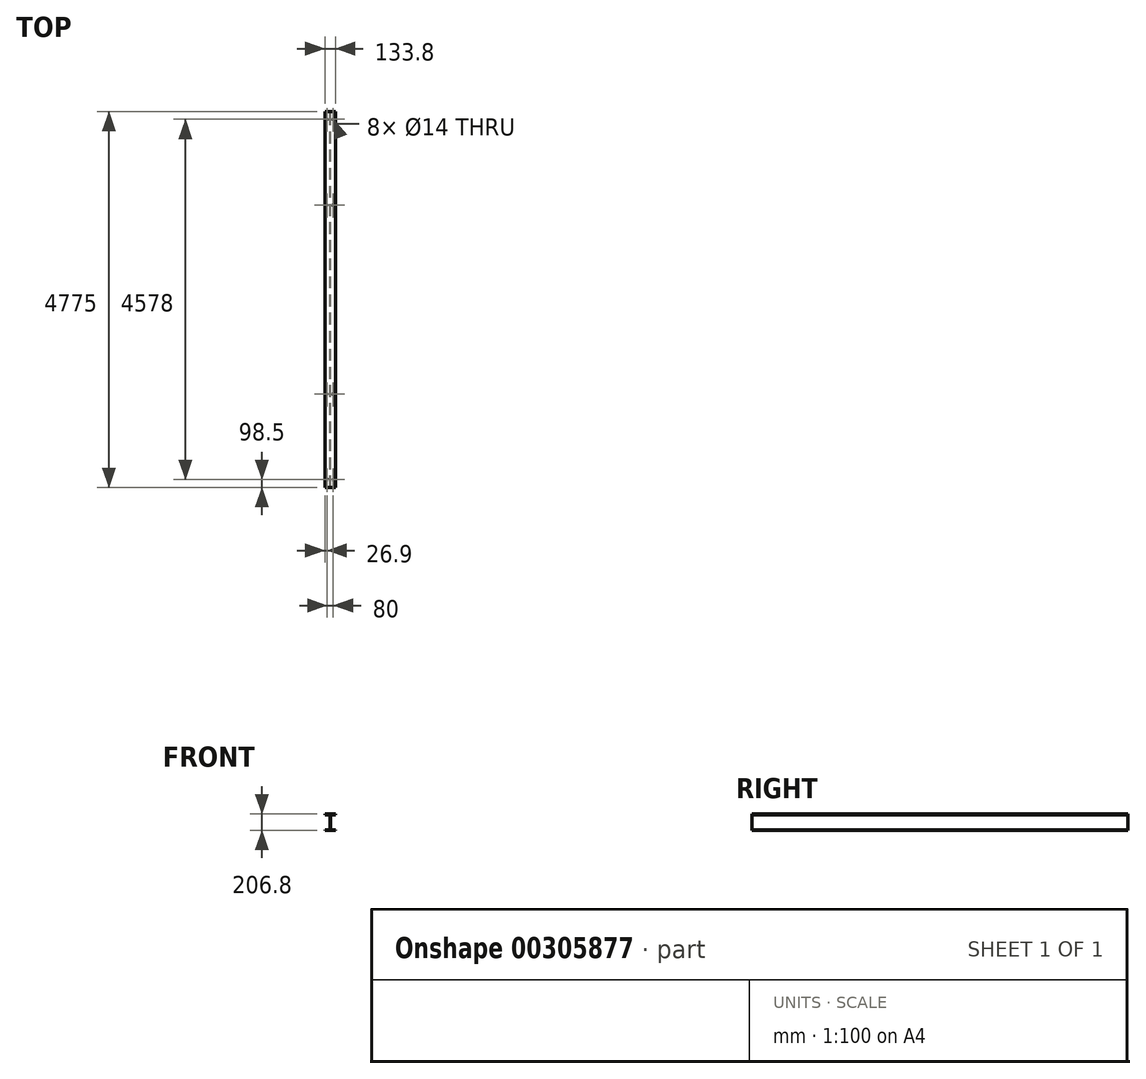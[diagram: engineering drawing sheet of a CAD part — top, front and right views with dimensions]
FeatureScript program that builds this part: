
annotation { "Feature Type Name" : "Feature", "Feature Type Description" : "" }
export const myFeature = defineFeature(function(context is Context, id is Id, definition is map)
    precondition{}
    {
        {
            var Q0;
            Q0=qCreatedBy(makeId("Front.planeOp"),FACE);
            var sketch = newSketch(context, id + "F0", { "sketchPlane" : qUnion([Q0])});
            skLineSegment(sketch, "E0.bottom", {"start": v(3.15, -24.05) * mm, "end": v(-3.15, -24.05) * mm});
            skLineSegment(sketch, "E0.top", {"start": v(3.15, 182.75) * mm, "end": v(-3.15, 182.75) * mm});
            skLineSegment(sketch, "E0.left", {"start": v(3.15, -24.05) * mm, "end": v(3.15, 182.75) * mm});
            skLineSegment(sketch, "E0.right", {"start": v(-3.15, -24.05) * mm, "end": v(-3.15, 182.75) * mm});
            skPoint(sketch, "E0.middle", {"position": v(0, 79.35) * mm});
            skLineSegment(sketch, "E1", {"start": v(0, 182.75) * mm, "end": v(0, 177.95) * mm, "construction": true});
            skLineSegment(sketch, "E2", {"start": v(0, -24.05) * mm, "end": v(0, -19.25) * mm, "construction": true});
            skLineSegment(sketch, "E3.bottom", {"start": v(66.9, 182.75) * mm, "end": v(-66.9, 182.75) * mm});
            skLineSegment(sketch, "E3.top", {"start": v(66.9, 173.15) * mm, "end": v(-66.9, 173.15) * mm});
            skLineSegment(sketch, "E3.left", {"start": v(66.9, 182.75) * mm, "end": v(66.9, 173.15) * mm});
            skLineSegment(sketch, "E3.right", {"start": v(-66.9, 182.75) * mm, "end": v(-66.9, 173.15) * mm});
            skPoint(sketch, "E3.middle", {"position": v(0, 177.95) * mm});
            skLineSegment(sketch, "E4.bottom", {"start": v(66.9, -24.05) * mm, "end": v(-66.9, -24.05) * mm});
            skLineSegment(sketch, "E4.top", {"start": v(66.9, -14.45) * mm, "end": v(-66.9, -14.45) * mm});
            skLineSegment(sketch, "E4.left", {"start": v(66.9, -24.05) * mm, "end": v(66.9, -14.45) * mm});
            skLineSegment(sketch, "E4.right", {"start": v(-66.9, -24.05) * mm, "end": v(-66.9, -14.45) * mm});
            skPoint(sketch, "E4.middle", {"position": v(0, -19.25) * mm});
            skSolve(sketch);
        }
        {
            var Q0;
            {var subQ5=sQuery(id+"F0.wireOp",EDGE,"E3.left");Q0=makeQuery(id+"F0.imprint","IMPRINT",FACE,{"disambiguationData":[TD([[makeQuery(id+"F0.imprint","IMPRINT",EDGE,{"derivedFrom":subQ5}),-1.0]])]});}
            var Q1;
            {var subQ5=sQuery(id+"F0.wireOp",EDGE,"E3.right");Q1=makeQuery(id+"F0.imprint","IMPRINT",FACE,{"disambiguationData":[TD([[makeQuery(id+"F0.imprint","IMPRINT",EDGE,{"derivedFrom":subQ5}),1.0]])]});}
            var Q2;
            {var subQ0=sQuery(id+"F0.wireOp",EDGE,"E3.bottom");var subQ1=sQuery(id+"F0.wireOp",EDGE,"E0.left");var subQ2=makeQuery(id+"F0.imprint","INTERSECT",VERTEX,{"derivedFrom":[subQ1,subQ0]});Q2=makeQuery(id+"F0.imprint","IMPRINT",FACE,{"disambiguationData":[TD([[makeQuery(id+"F0.imprint","IMPRINT",EDGE,{"disambiguationData":[TD([[subQ2,1.0]])],"derivedFrom":subQ1}),1.0]])]});}
            var Q3;
            {var subQ0=sQuery(id+"F0.wireOp",EDGE,"E4.top");var subQ1=sQuery(id+"F0.wireOp",EDGE,"E0.left");var subQ2=makeQuery(id+"F0.imprint","INTERSECT",VERTEX,{"derivedFrom":[subQ1,subQ0]});Q3=makeQuery(id+"F0.imprint","IMPRINT",FACE,{"disambiguationData":[TD([[makeQuery(id+"F0.imprint","IMPRINT",EDGE,{"disambiguationData":[TD([[subQ2,-1.0]])],"derivedFrom":subQ1}),1.0]])]});}
            var Q4;
            {var subQ5=sQuery(id+"F0.wireOp",EDGE,"E4.right");Q4=makeQuery(id+"F0.imprint","IMPRINT",FACE,{"disambiguationData":[TD([[makeQuery(id+"F0.imprint","IMPRINT",EDGE,{"derivedFrom":subQ5}),-1.0]])]});}
            var Q5;
            {var subQ0=sQuery(id+"F0.wireOp",EDGE,"E4.bottom");var subQ1=sQuery(id+"F0.wireOp",EDGE,"E0.left");var subQ2=makeQuery(id+"F0.imprint","INTERSECT",VERTEX,{"derivedFrom":[subQ1,subQ0]});Q5=makeQuery(id+"F0.imprint","IMPRINT",FACE,{"disambiguationData":[TD([[makeQuery(id+"F0.imprint","IMPRINT",EDGE,{"disambiguationData":[TD([[subQ2,-1.0]])],"derivedFrom":subQ1}),1.0]])]});}
            var Q6;
            {var subQ5=sQuery(id+"F0.wireOp",EDGE,"E4.left");Q6=makeQuery(id+"F0.imprint","IMPRINT",FACE,{"disambiguationData":[TD([[makeQuery(id+"F0.imprint","IMPRINT",EDGE,{"derivedFrom":subQ5}),1.0]])]});}
            extrude(context, id + "F1", {"entities" : qUnion([Q0, Q1, Q2, Q3, Q4, Q5, Q6]), "depth" : 4775 * mm});
        }
        {
            var Q0;
            Q0=makeQuery(id+"F1.opExtrude","SWEPT_FACE",FACE,{"disambiguationData":[OSD([sQuery(id+"F0.wireOp",EDGE,"E3.bottom")])]});
            var sketch = newSketch(context, id + "F2", { "sketchPlane" : qUnion([Q0])});
            skLineSegment(sketch, "E5.bottom", {"start": v(72.5, -4887.5) * mm, "end": v(-72.5, -4887.5) * mm});
            skLineSegment(sketch, "E5.top", {"start": v(72.5, 112.5) * mm, "end": v(-72.5, 112.5) * mm});
            skLineSegment(sketch, "E5.left", {"start": v(72.5, -4887.5) * mm, "end": v(72.5, 112.5) * mm});
            skLineSegment(sketch, "E5.right", {"start": v(-72.5, -4887.5) * mm, "end": v(-72.5, 112.5) * mm});
            skPoint(sketch, "E5.middle", {"position": v(0, -2387.5) * mm});
            skPoint(sketch, "E5.middle.positionSnap0", {"position": v(66.9, -2387.5) * mm});
            skPoint(sketch, "E5.centerSnap0", {"position": v(66.9, -2387.5) * mm});
            skLineSegment(sketch, "E6.bottom", {"start": v(40, -4887.5) * mm, "end": v(-40, -4887.5) * mm, "construction": true});
            skLineSegment(sketch, "E6.top", {"start": v(40, 112.5) * mm, "end": v(-40, 112.5) * mm, "construction": true});
            skLineSegment(sketch, "E6.left", {"start": v(40, -4887.5) * mm, "end": v(40, 112.5) * mm, "construction": true});
            skLineSegment(sketch, "E6.right", {"start": v(-40, -4887.5) * mm, "end": v(-40, 112.5) * mm, "construction": true});
            skLineSegment(sketch, "E7", {"start": v(-40, -1187.5) * mm, "end": v(40, -1187.5) * mm, "construction": true});
            skLineSegment(sketch, "E8", {"start": v(-40, -98.5) * mm, "end": v(40, -98.5) * mm, "construction": true});
            skLineSegment(sketch, "E9", {"start": v(-72.5, -2387.5) * mm, "end": v(72.5, -2387.5) * mm, "construction": true});
            skLineSegment(sketch, "E10.MirrorCS", {"start": v(-40, -3587.5) * mm, "end": v(40, -3587.5) * mm, "construction": true});
            skLineSegment(sketch, "E11.MirrorCS", {"start": v(-40, -4676.5) * mm, "end": v(40, -4676.5) * mm, "construction": true});
            skSolve(sketch);
        }
        {
            var Q0;
            Q0=sQuery(id+"F2.wireOp",VERTEX,"E8.start");
            var Q1;
            Q1=sQuery(id+"F2.wireOp",VERTEX,"E8.end");
            var Q2;
            Q2=sQuery(id+"F2.wireOp",VERTEX,"E7.start");
            var Q3;
            Q3=sQuery(id+"F2.wireOp",VERTEX,"E7.end");
            var Q4;
            Q4=sQuery(id+"F2.wireOp",VERTEX,"E10.MirrorCS.start");
            var Q5;
            Q5=sQuery(id+"F2.wireOp",VERTEX,"E10.MirrorCS.end");
            var Q6;
            Q6=sQuery(id+"F2.wireOp",VERTEX,"E11.MirrorCS.start");
            var Q7;
            Q7=sQuery(id+"F2.wireOp",VERTEX,"E11.MirrorCS.end");
            var Q8;
            Q8=makeQuery(id+"F1.opExtrude","SWEPT_BODY",BODY,{"disambiguationData":[OSD([sQuery(id+"F0.wireOp",EDGE,"E0.left"),sQuery(id+"F0.wireOp",EDGE,"E0.right"),sQuery(id+"F0.wireOp",EDGE,"E3.bottom"),sQuery(id+"F0.wireOp",EDGE,"E3.top"),sQuery(id+"F0.wireOp",EDGE,"E3.left"),sQuery(id+"F0.wireOp",EDGE,"E3.right"),sQuery(id+"F0.wireOp",EDGE,"E4.bottom"),sQuery(id+"F0.wireOp",EDGE,"E4.top"),sQuery(id+"F0.wireOp",EDGE,"E4.left"),sQuery(id+"F0.wireOp",EDGE,"E4.right")])]});
            hole(context, id + "F3", {"style" : HoleStyle.SIMPLE, "endStyle" : HoleEndStyle.BLIND, "holeDiameter" : 14 * mm, "holeDepth" : 10 * mm, "isTappedThrough" : true, "tappedDepth" : 12 * mm, "tapClearance" : 3, "locations" : qUnion([Q0, Q1, Q2, Q3, Q4, Q5, Q6, Q7]), "scope" : qUnion([Q8])});
        }
    });
